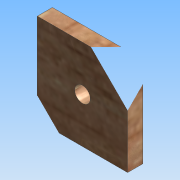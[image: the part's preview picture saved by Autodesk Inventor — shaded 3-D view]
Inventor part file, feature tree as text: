
AUTODESK INVENTOR PART (.ipt)
format: ipt  version: 2015 (Build 190159000, 159)  size: 93,184 bytes
history: native  units: mm
features: extrude x1, sketch x1
ambient origin geometry x8: Origin, YZ Plane, XZ Plane, XY Plane, X Axis, Y Axis, Z Axis, Center Point
bodies: Body1 (feature_tree)
feature tree (2):
  extrude  "Extrusion2"  Depth=30.0mm
  sketch  "Sketch1"  dims[d2=30.0mm d3=30.0mm d4=5.2mm d5=5.0mm d6=0.0mm]
